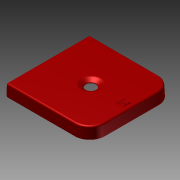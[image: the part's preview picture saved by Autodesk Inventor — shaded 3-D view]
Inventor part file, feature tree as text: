
AUTODESK INVENTOR PART (.ipt)
format: ipt  version: 2013 (Build 170138000, 138)  size: 374,784 bytes
history: native  units: in
note: dims shown in document units (in); Inventor stores cm internally (conversion verified against a paired STEP export)
features: fillet x7, plane x5, sketch x4, extrude x2, reference x2, draft x1, shell x1, mirror x1, hole x1, emboss x1
ambient origin geometry x8: Origin, YZ Plane, XZ Plane, XY Plane, X Axis, Y Axis, Z Axis, Center Point
feature tree (25):
  plane  "Work Plane1"
  plane  "Work Plane2"
  sketch  "Sketch2"  dims[d7=0.252in d8=0.0in d12=0.0137in d13=0.354in d14=0.071in]
  plane  "Work Plane3"
  extrude  "Extrusion3"  Depth=0.0137in
  plane  "Work Plane4"
  draft  "FaceDraft3"
  fillet  "Fillet5"  Radius=0.354in
  shell  "Shell1"  Thickness=0.071in
  extrude  "Extrusion4"  Depth=0.217in
  fillet  "Fillet6"  Radius=0.071in
  plane  "Work Plane5"
  mirror  "Mirror1"
  hole  "Hole1"  [1 undecoded]
  fillet  "Fillet7"  Radius=0.236in
  fillet  "Fillet8"  Radius=0.02in
  fillet  "Fillet9"  Radius=0.079in
  fillet  "Fillet10"  Radius=0.039in
  fillet  "Fillet11"  Radius=0.039in
  emboss  "Emboss1"
  reference  "Reference3"
  sketch  "Sketch4"  dims[d15=0.01in d16=0.217in d17=0.071in]
  sketch  "Sketch6"  dims[d18=0.252in d19=0.0in d20=0.02in d24=0.236in]
  reference  "Reference4"
  sketch  "Sketch7"  dims[d30=0.236in d31=0.75in d32=0.433in d33=0.25in d34=120.0deg d35=0.125in d36=0.8108in d37=0.02in d38=0.079in d39=0.039in d40=0.039in d41=0.02in d43=0.008in d44=0.0in]
note: 1 required parameter value undecoded (feature->parameter linkage not recoverable at this tier; creation-order binding heuristic only, values carry confidence <= 0.55)
